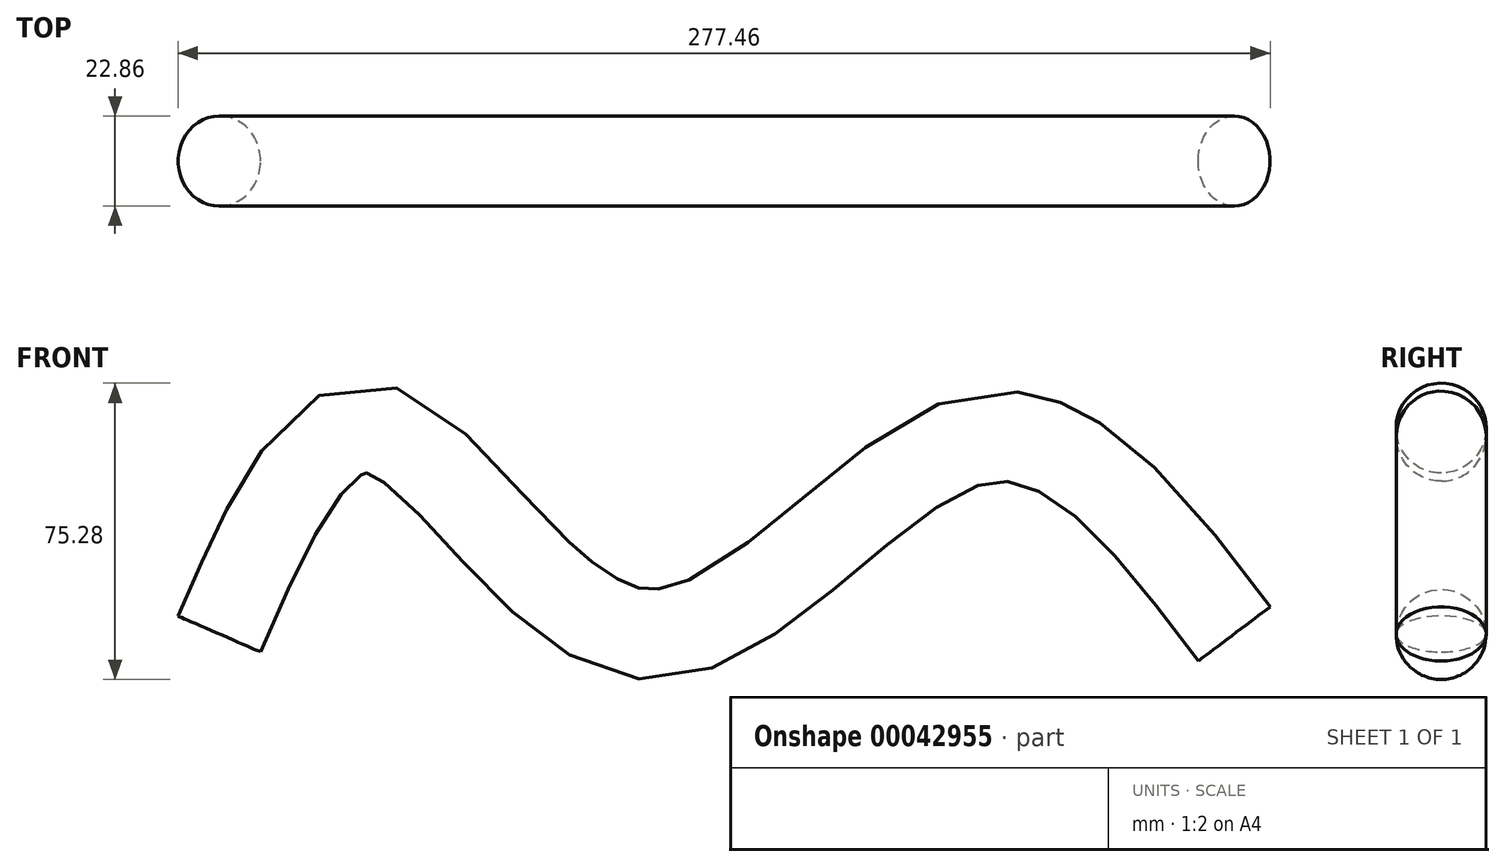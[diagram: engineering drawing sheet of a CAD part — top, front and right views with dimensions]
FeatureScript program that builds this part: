
annotation { "Feature Type Name" : "Feature", "Feature Type Description" : "" }
export const myFeature = defineFeature(function(context is Context, id is Id, definition is map)
    precondition{}
    {
        {
            var Q0;
            Q0=qCreatedBy(makeId("Front.planeOp"),FACE);
            var sketch = newSketch(context, id + "F0", { "sketchPlane" : qUnion([Q0])});
            skFitSpline(sketch, "E0", {"points": [v(-129.41, 0) * mm, v(-89.21, 51.96) * mm, v(-22.06, 0) * mm, v(62.74, 49.5) * mm, v(128.43, 0) * mm], "startDerivative": vector(162.58, 374.1) * mm, "endDerivative": vector(248.92, -331.7) * mm});
            skSolve(sketch);
        }
        {
            var Q0;
            Q0=sQuery(id+"F0.wireOp",EDGE,"E0");
            var Q1;
            Q1=sQuery(id+"F0.wireOp",VERTEX,"E0.end");
            cPlane(context, id + "F1", {"entities" : qUnion([Q0, Q1]), "cplaneType" : CPlaneType.CURVE_POINT, "offset" : 25 * mm, "width" : 150 * mm, "height" : 150 * mm});
        }
        {
            var Q0;
            Q0=qCreatedBy(id+"F1.planeOp",FACE);
            var sketch = newSketch(context, id + "F2", { "sketchPlane" : qUnion([Q0])});
            skCircle(sketch, "E1", {"center": v(102.72, 0) * mm, "radius": 11.43 * mm});
            skSolve(sketch);
        }
        {
            var Q0;
            Q0=makeQuery(id+"F2.imprint","IMPRINT",FACE,{"disambiguationData":[TD([[makeQuery(id+"F2.imprint","IMPRINT",EDGE,{"derivedFrom":sQuery(id+"F2.wireOp",EDGE,"E1")}),1.0]])]});
            var Q1;
            Q1=sQuery(id+"F0.wireOp",EDGE,"E0");
            sweep(context, id + "F3", {"profiles" : qUnion([Q0]), "path" : qUnion([Q1])});
        }
    });
